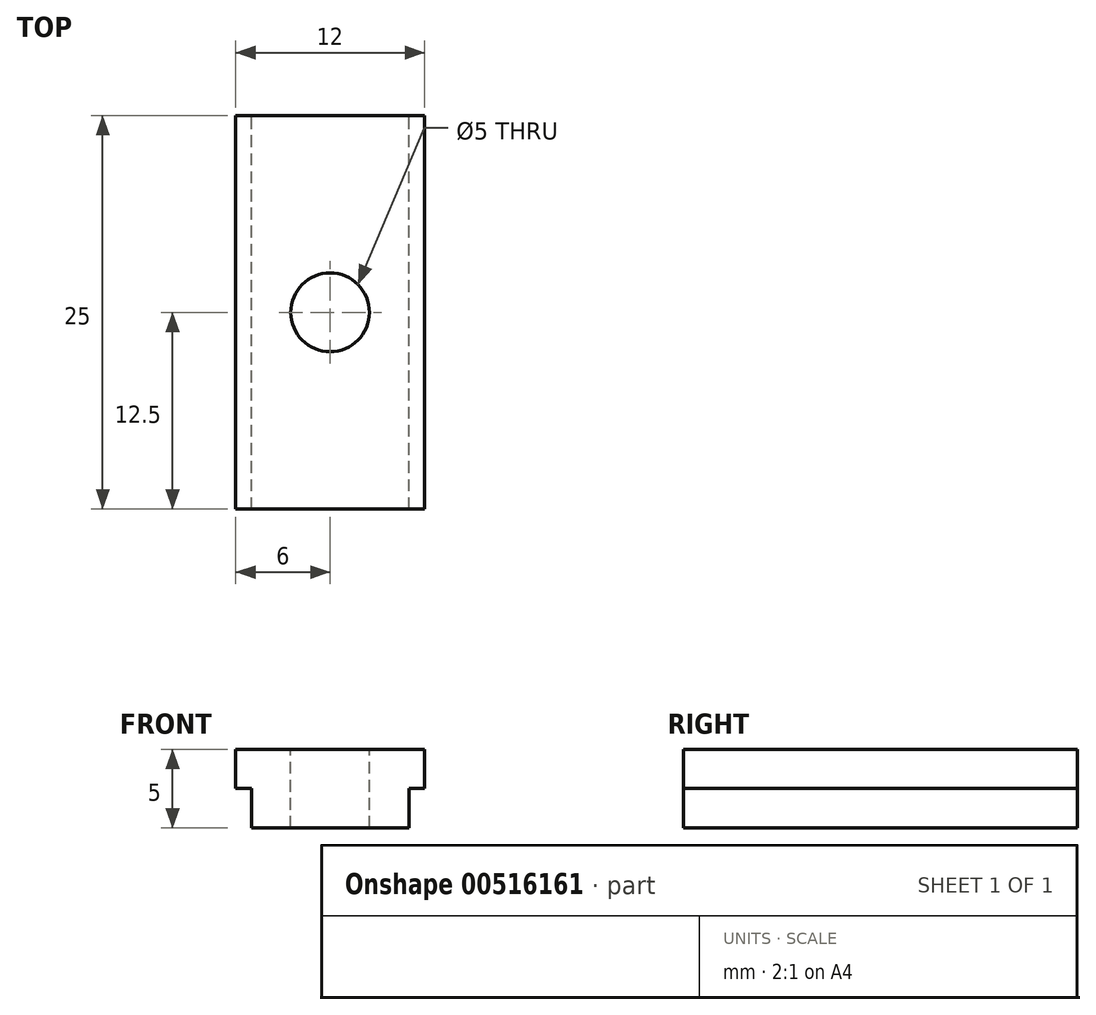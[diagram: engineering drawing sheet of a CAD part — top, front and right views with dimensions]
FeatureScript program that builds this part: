
annotation { "Feature Type Name" : "Feature", "Feature Type Description" : "" }
export const myFeature = defineFeature(function(context is Context, id is Id, definition is map)
    precondition{}
    {
        {
            var Q0;
            Q0=qCreatedBy(makeId("Front.planeOp"),FACE);
            var sketch = newSketch(context, id + "F0", { "sketchPlane" : qUnion([Q0])});
            skLineSegment(sketch, "E0", {"start": v(0, 5.64) * mm, "end": v(6, 5.64) * mm});
            skLineSegment(sketch, "E1", {"start": v(6, 5.64) * mm, "end": v(6, 3.14) * mm});
            skLineSegment(sketch, "E2", {"start": v(6, 3.14) * mm, "end": v(5, 3.14) * mm});
            skLineSegment(sketch, "E3", {"start": v(5, 3.14) * mm, "end": v(5, 0.64) * mm});
            skLineSegment(sketch, "E4", {"start": v(5, 0.64) * mm, "end": v(0, 0.64) * mm});
            skLineSegment(sketch, "E5", {"start": v(0, 0.64) * mm, "end": v(0, 5.64) * mm});
            skLineSegment(sketch, "E6.MirrorCS", {"start": v(-6, 3.14) * mm, "end": v(-5, 3.14) * mm});
            skLineSegment(sketch, "E7.MirrorCS", {"start": v(-6, 5.64) * mm, "end": v(-6, 3.14) * mm});
            skLineSegment(sketch, "E8.MirrorCS", {"start": v(-5, 3.14) * mm, "end": v(-5, 0.64) * mm});
            skLineSegment(sketch, "E9.MirrorCS", {"start": v(0, 5.64) * mm, "end": v(-6, 5.64) * mm});
            skLineSegment(sketch, "E10.MirrorCS", {"start": v(-5, 0.64) * mm, "end": v(0, 0.64) * mm});
            skSolve(sketch);
        }
        {
            var Q0;
            Q0 = qSketchRegion(id + "F0", true);
            extrude(context, id + "F1", {"entities" : qUnion([Q0]), "depth" : 25 * mm, "offsetDistance" : 25 * mm});
        }
        {
            var Q0;
            Q0=makeQuery(id+"F1.opExtrude","SWEPT_FACE",FACE,{"disambiguationData":[OSD([sQuery(id+"F0.wireOp",EDGE,"E0"),sQuery(id+"F0.wireOp",EDGE,"E9.MirrorCS")])]});
            var sketch = newSketch(context, id + "F2", { "sketchPlane" : qUnion([Q0])});
            skCircle(sketch, "E11", {"center": v(0, -12.5) * mm, "radius": 2.5 * mm});
            skSolve(sketch);
        }
        {
            var Q0;
            Q0=makeQuery(id+"F2.imprint","IMPRINT",FACE,{"disambiguationData":[TD([[makeQuery(id+"F2.imprint","IMPRINT",EDGE,{"derivedFrom":sQuery(id+"F2.wireOp",EDGE,"E11")}),1.0]])]});
            extrude(context, id + "F3", {"entities" : qUnion([Q0]), "operationType" : NewBodyOperationType.REMOVE, "oppositeDirection" : true, "depth" : 25 * mm, "offsetDistance" : 25 * mm});
        }
    });
